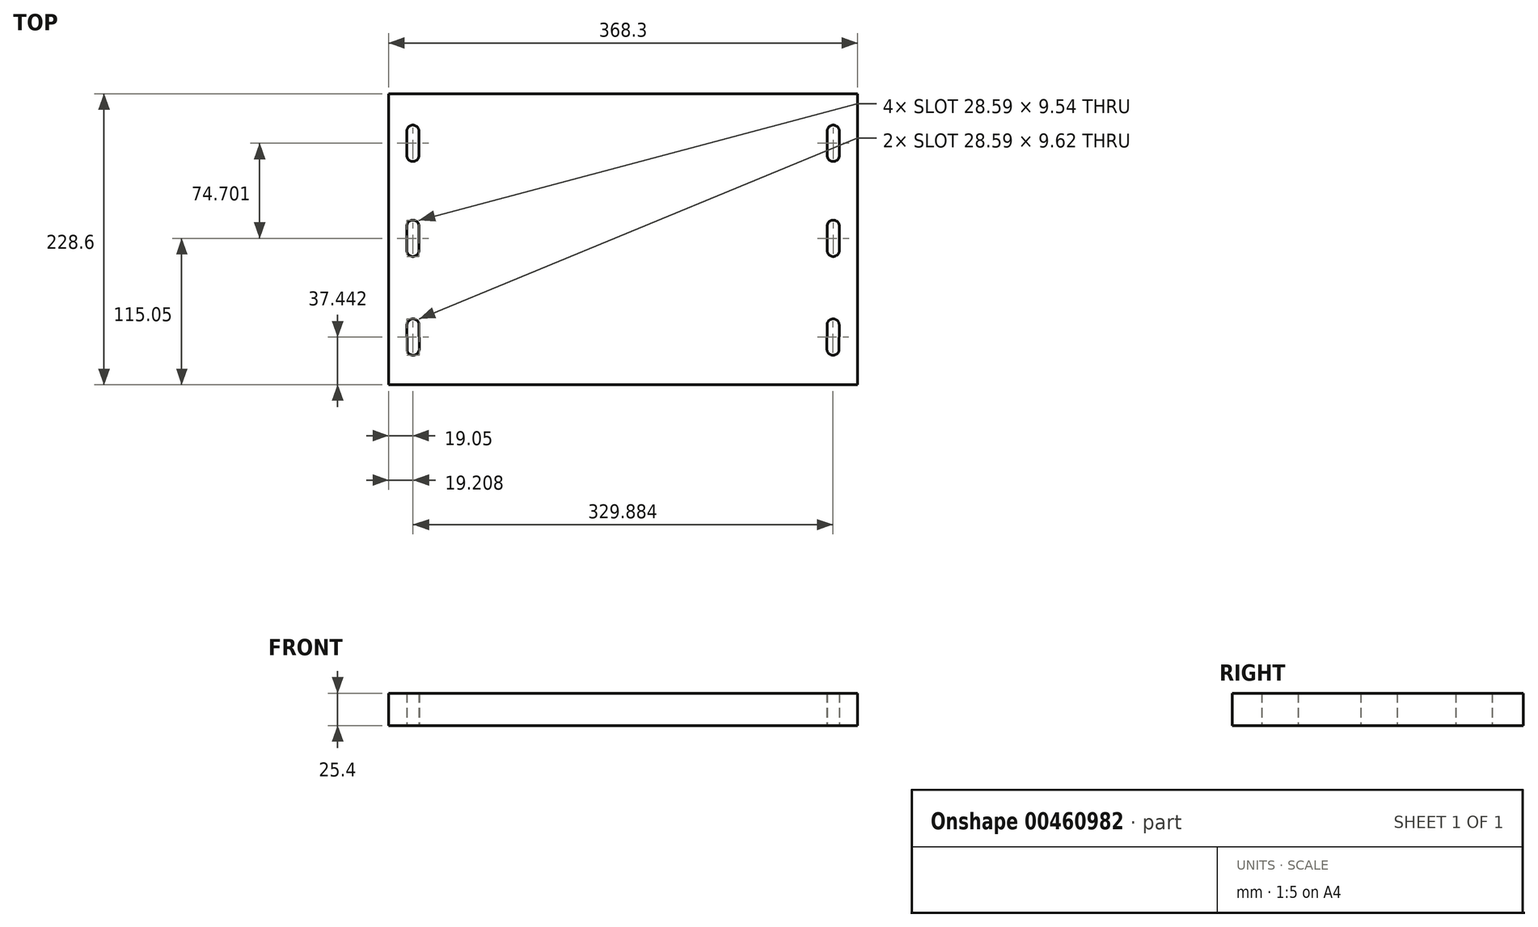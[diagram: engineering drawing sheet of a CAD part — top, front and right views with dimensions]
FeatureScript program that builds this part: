
annotation { "Feature Type Name" : "Feature", "Feature Type Description" : "" }
export const myFeature = defineFeature(function(context is Context, id is Id, definition is map)
    precondition{}
    {
        {
            var Q0;
            Q0=qCreatedBy(makeId("Top.planeOp"),FACE);
            var sketch = newSketch(context, id + "F0", { "sketchPlane" : qUnion([Q0])});
            skLineSegment(sketch, "E0.bottom", {"start": v(-235.04, 113.55) * mm, "end": v(133.26, 113.55) * mm});
            skLineSegment(sketch, "E0.top", {"start": v(-235.04, -115.05) * mm, "end": v(133.26, -115.05) * mm});
            skLineSegment(sketch, "E0.left", {"start": v(-235.04, 113.55) * mm, "end": v(-235.04, -115.05) * mm});
            skLineSegment(sketch, "E0.right", {"start": v(133.26, 113.55) * mm, "end": v(133.26, -115.05) * mm});
            skArc(sketch, "E1.0.startCap", {"start": v(-220.76, 9.52) * mm, "mid": v(-215.99, 14.3) * mm, "end": v(-211.22, 9.52) * mm});
            skArc(sketch, "E1.0.endCap", {"start": v(-211.22, -9.53) * mm, "mid": v(-215.99, -14.3) * mm, "end": v(-220.76, -9.53) * mm});
            skLineSegment(sketch, "E1.0.left", {"start": v(-211.22, 9.52) * mm, "end": v(-211.22, -9.53) * mm});
            skLineSegment(sketch, "E1.0.right", {"start": v(-220.76, 9.52) * mm, "end": v(-220.76, -9.53) * mm});
            skLineSegment(sketch, "E2.MirrorCS", {"start": v(-211.33, 65.29) * mm, "end": v(-211.41, 84.34) * mm});
            skArc(sketch, "E3.MirrorCS", {"start": v(-220.87, 65.25) * mm, "mid": v(-216.08, 60.5) * mm, "end": v(-211.33, 65.29) * mm});
            skLineSegment(sketch, "E4.MirrorCS", {"start": v(-220.87, 65.25) * mm, "end": v(-220.95, 84.3) * mm});
            skArc(sketch, "E5.MirrorCS", {"start": v(-211.22, 84.34) * mm, "mid": v(-216, 89.09) * mm, "end": v(-220.76, 84.3) * mm});
            skArc(sketch, "E6.MirrorCS", {"start": v(-211.1, -68.06) * mm, "mid": v(-215.9, -63.31) * mm, "end": v(-220.64, -68.1) * mm});
            skLineSegment(sketch, "E7.MirrorCS", {"start": v(-211.02, -87.11) * mm, "end": v(-211.1, -68.06) * mm});
            skLineSegment(sketch, "E8.MirrorCS", {"start": v(-220.56, -87.15) * mm, "end": v(-220.64, -68.1) * mm});
            skArc(sketch, "E9.MirrorCS", {"start": v(-220.56, -87.15) * mm, "mid": v(-215.77, -91.9) * mm, "end": v(-211.02, -87.11) * mm});
            skArc(sketch, "E10.MirrorCS", {"start": v(109.44, 84.34) * mm, "mid": v(114.23, 89.09) * mm, "end": v(118.98, 84.3) * mm});
            skLineSegment(sketch, "E11.MirrorCS", {"start": v(119.1, 65.25) * mm, "end": v(119.17, 84.3) * mm});
            skLineSegment(sketch, "E12.MirrorCS", {"start": v(109.55, 65.29) * mm, "end": v(109.63, 84.34) * mm});
            skArc(sketch, "E13.MirrorCS", {"start": v(119.1, 65.25) * mm, "mid": v(114.3, 60.5) * mm, "end": v(109.55, 65.29) * mm});
            skArc(sketch, "E14.MirrorCS", {"start": v(118.98, 9.52) * mm, "mid": v(114.21, 14.3) * mm, "end": v(109.44, 9.52) * mm});
            skLineSegment(sketch, "E15.MirrorCS", {"start": v(118.98, 9.52) * mm, "end": v(118.98, -9.53) * mm});
            skLineSegment(sketch, "E16.MirrorCS", {"start": v(109.44, 9.52) * mm, "end": v(109.44, -9.53) * mm});
            skArc(sketch, "E17.MirrorCS", {"start": v(109.44, -9.53) * mm, "mid": v(114.21, -14.3) * mm, "end": v(118.98, -9.53) * mm});
            skArc(sketch, "E18.MirrorCS", {"start": v(118.78, -87.15) * mm, "mid": v(114, -91.9) * mm, "end": v(109.24, -87.11) * mm});
            skLineSegment(sketch, "E19.MirrorCS", {"start": v(109.24, -87.11) * mm, "end": v(109.32, -68.06) * mm});
            skLineSegment(sketch, "E20.MirrorCS", {"start": v(118.78, -87.15) * mm, "end": v(118.86, -68.1) * mm});
            skArc(sketch, "E21.MirrorCS", {"start": v(109.32, -68.06) * mm, "mid": v(114.11, -63.31) * mm, "end": v(118.86, -68.1) * mm});
            skArc(sketch, "E22.MirrorCS", {"start": v(-220.76, 65.18) * mm, "mid": v(-215.99, 60.4) * mm, "end": v(-211.22, 65.18) * mm});
            skLineSegment(sketch, "E23.MirrorCS", {"start": v(-211.22, 65.18) * mm, "end": v(-211.22, 84.23) * mm});
            skLineSegment(sketch, "E24.MirrorCS", {"start": v(-220.76, 65.18) * mm, "end": v(-220.76, 84.23) * mm});
            skArc(sketch, "E25.MirrorCS", {"start": v(-211.22, 84.23) * mm, "mid": v(-215.99, 89) * mm, "end": v(-220.76, 84.23) * mm});
            skArc(sketch, "E26.MirrorCS", {"start": v(109.44, 84.23) * mm, "mid": v(114.21, 89) * mm, "end": v(118.98, 84.23) * mm});
            skLineSegment(sketch, "E27.MirrorCS", {"start": v(118.98, 65.18) * mm, "end": v(118.98, 84.23) * mm});
            skLineSegment(sketch, "E28.MirrorCS", {"start": v(109.44, 65.18) * mm, "end": v(109.44, 84.23) * mm});
            skArc(sketch, "E29.MirrorCS", {"start": v(118.98, 65.18) * mm, "mid": v(114.21, 60.4) * mm, "end": v(109.44, 65.18) * mm});
            skSolve(sketch);
        }
        {
            var Q0;
            Q0=makeQuery(id+"F0.imprint","IMPRINT",FACE,{"disambiguationData":[TD([[makeQuery(id+"F0.imprint","IMPRINT",EDGE,{"derivedFrom":sQuery(id+"F0.wireOp",EDGE,"E0.bottom")}),-1.0]])]});
            extrude(context, id + "F1", {"entities" : qUnion([Q0]), "depth" : 25.4 * mm, "offsetDistance" : 25.4 * mm});
        }
    });
